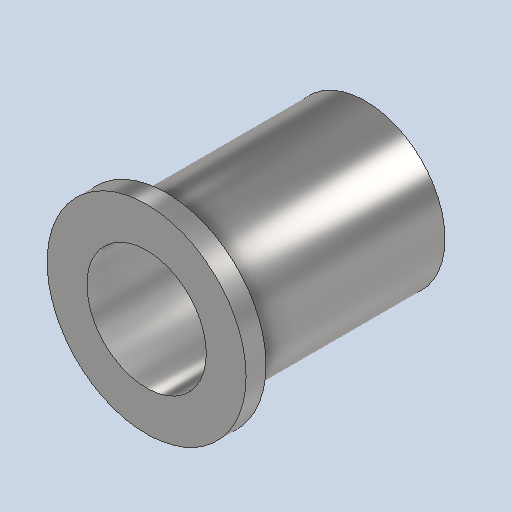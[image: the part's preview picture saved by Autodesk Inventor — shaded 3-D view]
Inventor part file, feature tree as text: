
AUTODESK INVENTOR PART (.ipt)
format: ipt  version: 2022.2 (Build 262287010, 287A)  size: 148,992 bytes
history: native  units: mm
features: extrude x2, sketch x2
ambient origin geometry x8: Origin, YZ Plane, XZ Plane, XY Plane, X Axis, Y Axis, Z Axis, Center Point
bodies: Solid1 (feature_tree)
feature tree (4):
  extrude  "Extrusion1"  Depth=6.0mm
  extrude  "Extrusion2"  Depth=10.0mm
  sketch  "Sketch1"  dims[d0=8.0mm d1=6.0mm]
  sketch  "Sketch2"  dims[d2=10.0mm d3=0.0mm d4=10.0mm d5=1.0mm d6=0.0mm]
